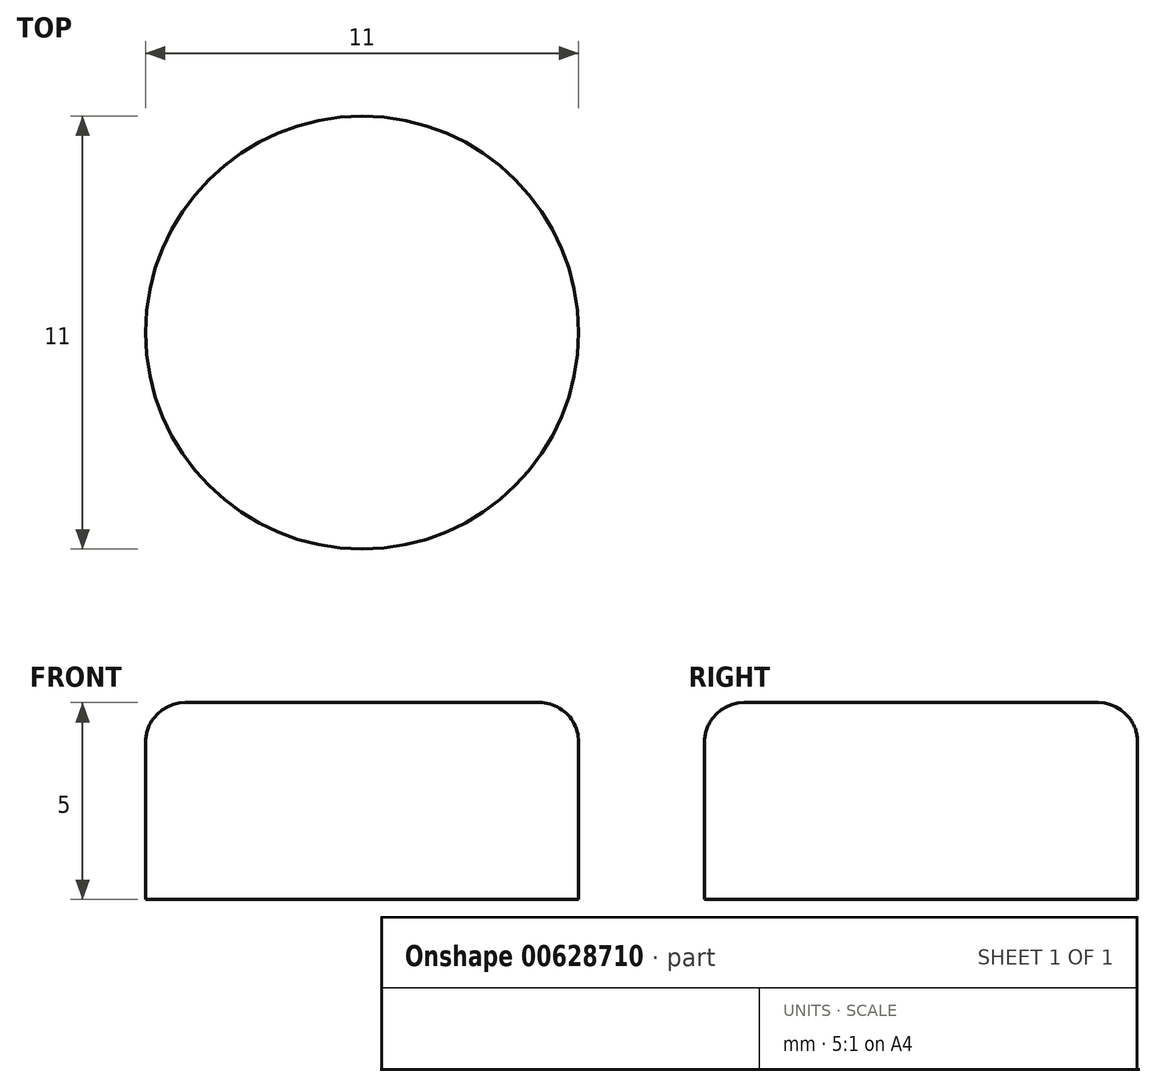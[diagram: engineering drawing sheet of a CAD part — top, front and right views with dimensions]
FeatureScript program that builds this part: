
annotation { "Feature Type Name" : "Feature", "Feature Type Description" : "" }
export const myFeature = defineFeature(function(context is Context, id is Id, definition is map)
    precondition{}
    {
        {
            var Q0;
            Q0=qCreatedBy(makeId("Top.planeOp"),FACE);
            var sketch = newSketch(context, id + "F0", { "sketchPlane" : qUnion([Q0])});
            skCircle(sketch, "E0", {"center": v(0, 0) * mm, "radius": 5.5 * mm});
            skSolve(sketch);
        }
        {
            var Q0;
            Q0 = qSketchRegion(id + "F0", true);
            extrude(context, id + "F1", {"entities" : qUnion([Q0]), "endBound" : BoundingType.SYMMETRIC, "depth" : 5 * mm, "offsetDistance" : 25 * mm});
        }
        {
            var Q0;
            Q0=makeQuery(id+"F1.opExtrude","CAP_EDGE",EDGE,{"disambiguationData":[OSD([sQuery(id+"F0.wireOp",EDGE,"E0")])],"isStart":false});
            fillet(context, id + "F2", {"entities" : qUnion([Q0]), "radius" : 1 * mm, "tangentPropagation" : true, "allowEdgeOverflow" : false});
        }
    });
